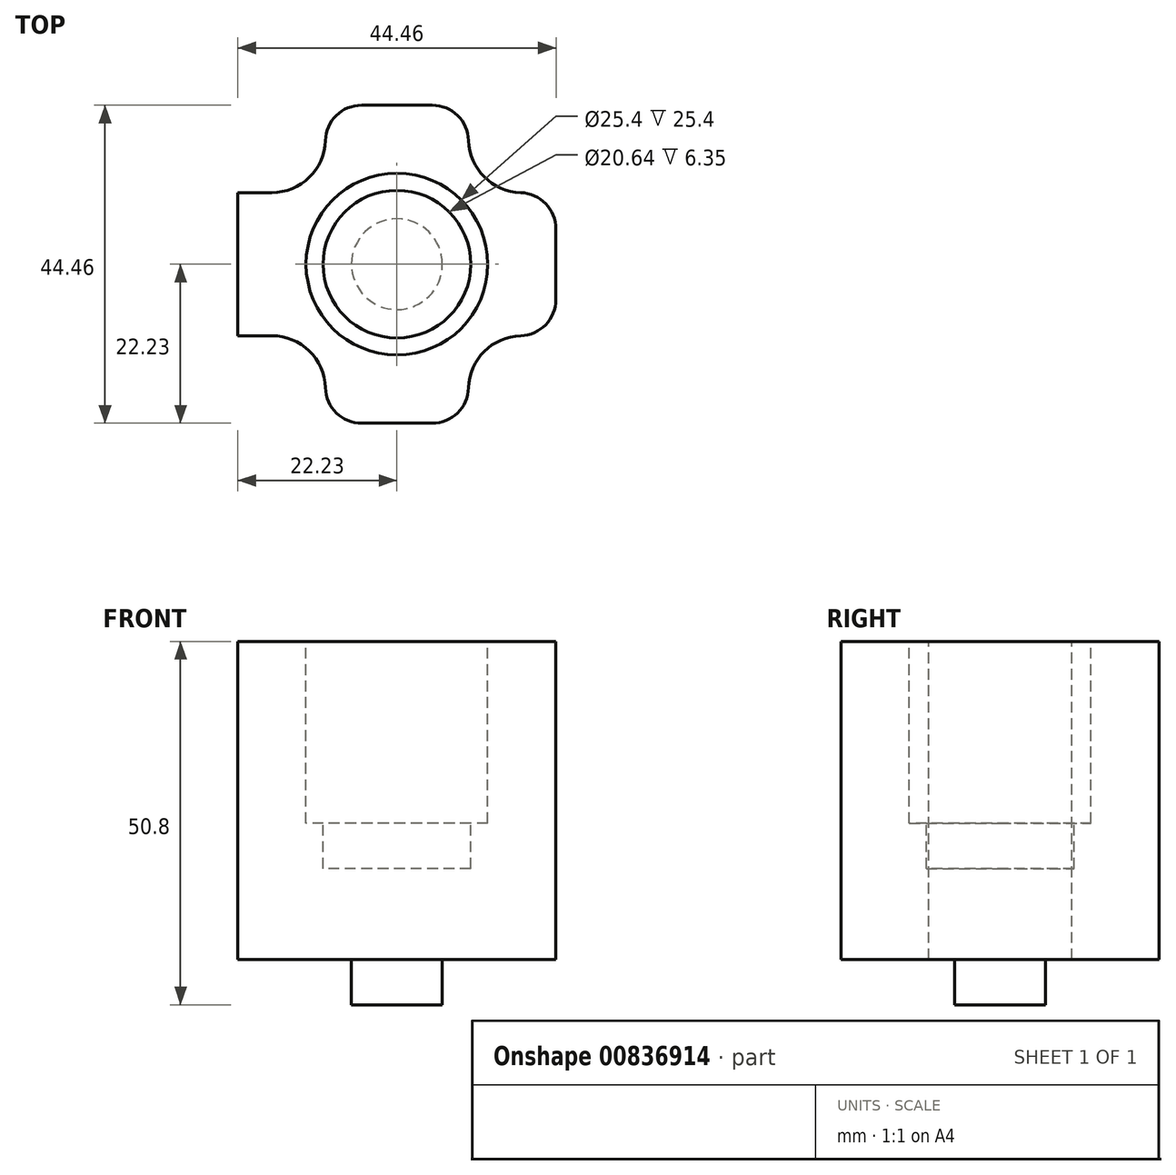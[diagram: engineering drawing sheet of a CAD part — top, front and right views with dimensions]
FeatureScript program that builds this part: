
annotation { "Feature Type Name" : "Feature", "Feature Type Description" : "" }
export const myFeature = defineFeature(function(context is Context, id is Id, definition is map)
    precondition{}
    {
        {
            var Q0;
            Q0=qCreatedBy(makeId("Top.planeOp"),FACE);
            var sketch = newSketch(context, id + "F0", { "sketchPlane" : qUnion([Q0])});
            skLineSegment(sketch, "E0.bottom", {"start": v(22.23, 22.22) * mm, "end": v(-22.23, 22.22) * mm});
            skLineSegment(sketch, "E0.top", {"start": v(22.23, -22.22) * mm, "end": v(-22.23, -22.22) * mm});
            skLineSegment(sketch, "E0.left", {"start": v(22.23, 22.23) * mm, "end": v(22.23, -22.22) * mm});
            skLineSegment(sketch, "E0.right", {"start": v(-22.23, 22.23) * mm, "end": v(-22.23, -22.22) * mm});
            skPoint(sketch, "E0.middle", {"position": v(0, 0) * mm});
            skSolve(sketch);
        }
        {
            var Q0;
            Q0 = qSketchRegion(id + "F0", true);
            extrude(context, id + "F1", {"entities" : qUnion([Q0]), "depth" : 44.45 * mm, "offsetDistance" : 25.4 * mm});
        }
        {
            var Q0;
            Q0=makeQuery(id+"F1.opExtrude","CAP_FACE",FACE,{"disambiguationData":[OSD([sQuery(id+"F0.wireOp",EDGE,"E0.bottom"),sQuery(id+"F0.wireOp",EDGE,"E0.top"),sQuery(id+"F0.wireOp",EDGE,"E0.left"),sQuery(id+"F0.wireOp",EDGE,"E0.right")])],"isStart":false});
            var sketch = newSketch(context, id + "F2", { "sketchPlane" : qUnion([Q0])});
            skCircle(sketch, "E1", {"center": v(0, 0) * mm, "radius": 10.32 * mm});
            skSolve(sketch);
        }
        {
            var Q0;
            Q0 = qSketchRegion(id + "F2", true);
            extrude(context, id + "F3", {"entities" : qUnion([Q0]), "operationType" : NewBodyOperationType.REMOVE, "oppositeDirection" : true, "depth" : 31.75 * mm, "offsetDistance" : 25.4 * mm});
        }
        {
            var Q0;
            Q0=makeQuery(id+"F1.opExtrude","CAP_FACE",FACE,{"disambiguationData":[OSD([sQuery(id+"F0.wireOp",EDGE,"E0.bottom"),sQuery(id+"F0.wireOp",EDGE,"E0.top"),sQuery(id+"F0.wireOp",EDGE,"E0.left"),sQuery(id+"F0.wireOp",EDGE,"E0.right")])],"isStart":false});
            var sketch = newSketch(context, id + "F4", { "sketchPlane" : qUnion([Q0])});
            skLineSegment(sketch, "E2.bottom", {"start": v(17.5, 17.5) * mm, "end": v(-17.5, 17.5) * mm, "construction": true});
            skLineSegment(sketch, "E2.top", {"start": v(17.5, -17.5) * mm, "end": v(-17.5, -17.5) * mm, "construction": true});
            skLineSegment(sketch, "E2.left", {"start": v(17.5, 17.5) * mm, "end": v(17.5, -17.5) * mm, "construction": true});
            skLineSegment(sketch, "E2.right", {"start": v(-17.5, 17.5) * mm, "end": v(-17.5, -17.5) * mm, "construction": true});
            skPoint(sketch, "E2.middle", {"position": v(0, 0) * mm});
            skCircle(sketch, "E3", {"center": v(-17.5, 17.5) * mm, "radius": 7.5 * mm});
            skCircle(sketch, "E4", {"center": v(17.5, 17.5) * mm, "radius": 7.5 * mm});
            skCircle(sketch, "E5", {"center": v(17.5, -17.5) * mm, "radius": 7.5 * mm});
            skCircle(sketch, "E6", {"center": v(-17.5, -17.5) * mm, "radius": 7.5 * mm});
            skSolve(sketch);
        }
        {
            var Q0;
            Q0 = qSketchRegion(id + "F4", true);
            extrude(context, id + "F5", {"entities" : qUnion([Q0]), "operationType" : NewBodyOperationType.REMOVE, "oppositeDirection" : true, "depth" : 50.8 * mm, "offsetDistance" : 25.4 * mm});
        }
        {
            var Q0;
            Q0=makeQuery(id+"F5.boolean.opBoolean","INTERSECT",EDGE,{"derivedFrom":[makeQuery(id+"F1.opExtrude","SWEPT_FACE",FACE,{"disambiguationData":[OSD([sQuery(id+"F0.wireOp",EDGE,"E0.top")])]}),makeQuery(id+"F5.opExtrude","SWEPT_FACE",FACE,{"disambiguationData":[OSD([sQuery(id+"F4.wireOp",EDGE,"E6")])]})]});
            var Q1;
            Q1=makeQuery(id+"F5.boolean.opBoolean","INTERSECT",EDGE,{"derivedFrom":[makeQuery(id+"F1.opExtrude","SWEPT_FACE",FACE,{"disambiguationData":[OSD([sQuery(id+"F0.wireOp",EDGE,"E0.top")])]}),makeQuery(id+"F5.opExtrude","SWEPT_FACE",FACE,{"disambiguationData":[OSD([sQuery(id+"F4.wireOp",EDGE,"E5")])]})]});
            var Q2;
            Q2=makeQuery(id+"F5.boolean.opBoolean","INTERSECT",EDGE,{"derivedFrom":[makeQuery(id+"F1.opExtrude","SWEPT_FACE",FACE,{"disambiguationData":[OSD([sQuery(id+"F0.wireOp",EDGE,"E0.left")])]}),makeQuery(id+"F5.opExtrude","SWEPT_FACE",FACE,{"disambiguationData":[OSD([sQuery(id+"F4.wireOp",EDGE,"E5")])]})]});
            var Q3;
            Q3=makeQuery(id+"F5.boolean.opBoolean","INTERSECT",EDGE,{"derivedFrom":[makeQuery(id+"F1.opExtrude","SWEPT_FACE",FACE,{"disambiguationData":[OSD([sQuery(id+"F0.wireOp",EDGE,"E0.bottom")])]}),makeQuery(id+"F5.opExtrude","SWEPT_FACE",FACE,{"disambiguationData":[OSD([sQuery(id+"F4.wireOp",EDGE,"E3")])]})]});
            var Q4;
            Q4=makeQuery(id+"F5.boolean.opBoolean","INTERSECT",EDGE,{"derivedFrom":[makeQuery(id+"F1.opExtrude","SWEPT_FACE",FACE,{"disambiguationData":[OSD([sQuery(id+"F0.wireOp",EDGE,"E0.bottom")])]}),makeQuery(id+"F5.opExtrude","SWEPT_FACE",FACE,{"disambiguationData":[OSD([sQuery(id+"F4.wireOp",EDGE,"E4")])]})]});
            var Q5;
            Q5=makeQuery(id+"F5.boolean.opBoolean","INTERSECT",EDGE,{"derivedFrom":[makeQuery(id+"F1.opExtrude","SWEPT_FACE",FACE,{"disambiguationData":[OSD([sQuery(id+"F0.wireOp",EDGE,"E0.left")])]}),makeQuery(id+"F5.opExtrude","SWEPT_FACE",FACE,{"disambiguationData":[OSD([sQuery(id+"F4.wireOp",EDGE,"E4")])]})]});
            fillet(context, id + "F6", {"entities" : qUnion([Q0, Q1, Q2, Q3, Q4, Q5]), "radius" : 5.08 * mm, "tangentPropagation" : true, "allowEdgeOverflow" : false});
        }
        {
            var Q0;
            Q0=makeQuery(id+"FQgiEi5B3x2nrJE_1.boolean.opBoolean","MERGE",FACE,{"derivedFrom":[makeQuery(id+"F1.opExtrude","CAP_FACE",FACE,{"disambiguationData":[OSD([sQuery(id+"F0.wireOp",EDGE,"E0.bottom"),sQuery(id+"F0.wireOp",EDGE,"E0.top"),sQuery(id+"F0.wireOp",EDGE,"E0.left"),sQuery(id+"F0.wireOp",EDGE,"E0.right")])],"isStart":false}),makeQuery(id+"FQgiEi5B3x2nrJE_1.opExtrude","CAP_FACE",FACE,{"disambiguationData":[OSD([sQuery(id+"FWA8kAkKu1zUJzs_1.wireOp",EDGE,"DTfPbG5I-5EFz-U5VQ-zpU0-isXJH0FyqWXz.bottom"),sQuery(id+"FWA8kAkKu1zUJzs_1.wireOp",EDGE,"DTfPbG5I-5EFz-U5VQ-zpU0-isXJH0FyqWXz.top"),sQuery(id+"FWA8kAkKu1zUJzs_1.wireOp",EDGE,"DTfPbG5I-5EFz-U5VQ-zpU0-isXJH0FyqWXz.left"),sQuery(id+"FWA8kAkKu1zUJzs_1.wireOp",EDGE,"DTfPbG5I-5EFz-U5VQ-zpU0-isXJH0FyqWXz.right"),sQuery(id+"FWA8kAkKu1zUJzs_1.wireOp",EDGE,"3J2amvpu-wV7f-ellf-ajKv-OtqYnOiRKbLl"),sQuery(id+"FWA8kAkKu1zUJzs_1.wireOp",EDGE,"7d3fb047-7b26-4dce-94f4-b0de5986607c.trimOffspring")])],"isStart":true})]});
            var sketch = newSketch(context, id + "F7", { "sketchPlane" : qUnion([Q0])});
            skLineSegment(sketch, "E7.bottom", {"start": v(-17.5, 10) * mm, "end": v(-22.23, 10) * mm});
            skLineSegment(sketch, "E7.top", {"start": v(-17.5, -10) * mm, "end": v(-22.23, -10) * mm});
            skLineSegment(sketch, "E8", {"start": v(-22.23, 10) * mm, "end": v(-22.23, 11.68) * mm});
            skLineSegment(sketch, "E9", {"start": v(-22.23, 11.68) * mm, "end": v(-17.5, 10) * mm});
            skLineSegment(sketch, "E10", {"start": v(-17.5, -10) * mm, "end": v(-22.23, -12.57) * mm});
            skLineSegment(sketch, "E11", {"start": v(-22.23, -12.57) * mm, "end": v(-22.23, -10) * mm});
            skSolve(sketch);
        }
        {
            var Q0;
            Q0 = qSketchRegion(id + "F7", true);
            extrude(context, id + "F8", {"entities" : qUnion([Q0]), "operationType" : NewBodyOperationType.REMOVE, "oppositeDirection" : true, "depth" : 50.8 * mm, "offsetDistance" : 25.4 * mm});
        }
        {
            var Q0;
            Q0=makeQuery(id+"Fhf0N23RiavLfdf_1.boolean.opBoolean","MERGE",FACE,{"derivedFrom":[makeQuery(id+"F1.opExtrude","CAP_FACE",FACE,{"disambiguationData":[OSD([sQuery(id+"F0.wireOp",EDGE,"E0.bottom"),sQuery(id+"F0.wireOp",EDGE,"E0.top"),sQuery(id+"F0.wireOp",EDGE,"E0.left"),sQuery(id+"F0.wireOp",EDGE,"E0.right")])],"isStart":true}),makeQuery(id+"Fhf0N23RiavLfdf_1.opExtrude","SWEPT_FACE",FACE,{"disambiguationData":[OSD([sQuery(id+"FqDmUrjYBAPfMIO_1.wireOp",EDGE,"DlPgtrbC-WDov-t1Tp-KwNC-MjAt0b3Ze47C.bottom")])]})]});
            var sketch = newSketch(context, id + "F9", { "sketchPlane" : qUnion([Q0])});
            skCircle(sketch, "E12", {"center": v(0, 0) * mm, "radius": 6.35 * mm});
            skSolve(sketch);
        }
        {
            var Q0;
            Q0 = qSketchRegion(id + "F9", true);
            extrude(context, id + "F10", {"entities" : qUnion([Q0]), "operationType" : NewBodyOperationType.ADD, "depth" : 6.35 * mm, "offsetDistance" : 25.4 * mm});
        }
        {
            var Q0;
            Q0=makeQuery(id+"F1.opExtrude","CAP_FACE",FACE,{"disambiguationData":[OSD([sQuery(id+"F0.wireOp",EDGE,"E0.bottom"),sQuery(id+"F0.wireOp",EDGE,"E0.top"),sQuery(id+"F0.wireOp",EDGE,"E0.left"),sQuery(id+"F0.wireOp",EDGE,"E0.right")])],"isStart":false});
            var sketch = newSketch(context, id + "F11", { "sketchPlane" : qUnion([Q0])});
            skCircle(sketch, "E13", {"center": v(0, 0) * mm, "radius": 12.7 * mm});
            skSolve(sketch);
        }
        {
            var Q0;
            Q0 = qSketchRegion(id + "F11", true);
            extrude(context, id + "F12", {"entities" : qUnion([Q0]), "operationType" : NewBodyOperationType.REMOVE, "oppositeDirection" : true, "depth" : 25.4 * mm, "offsetDistance" : 25.4 * mm});
        }
    });
